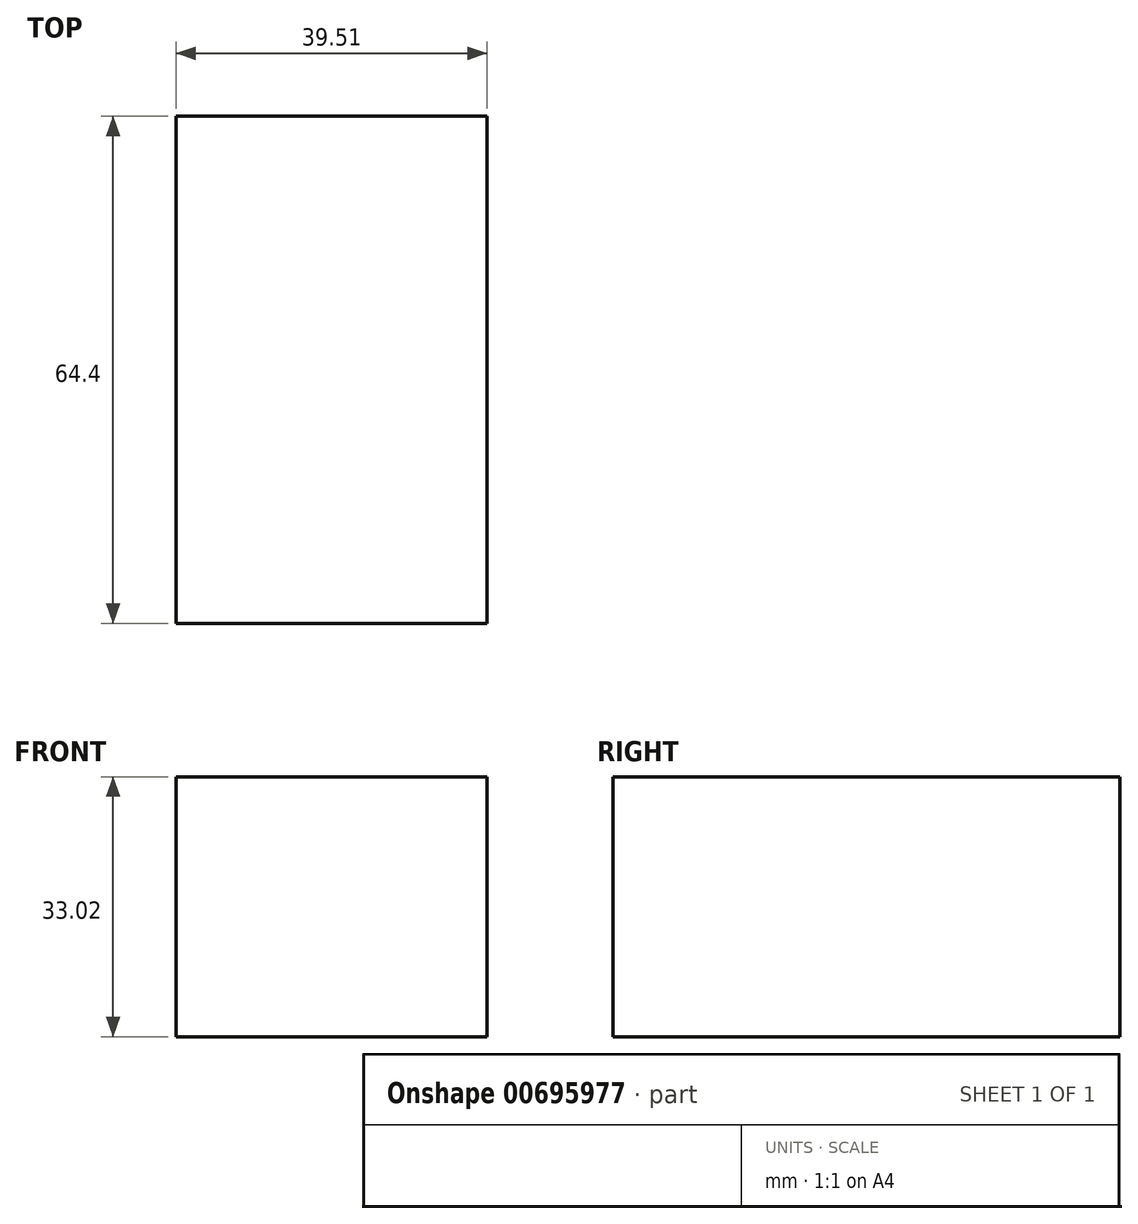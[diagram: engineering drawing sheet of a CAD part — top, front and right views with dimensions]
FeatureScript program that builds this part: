
annotation { "Feature Type Name" : "Feature", "Feature Type Description" : "" }
export const myFeature = defineFeature(function(context is Context, id is Id, definition is map)
    precondition{}
    {
        {
            var Q0;
            Q0=qCreatedBy(makeId("Top.planeOp"),FACE);
            var sketch = newSketch(context, id + "F0", { "sketchPlane" : qUnion([Q0])});
            skLineSegment(sketch, "E0.bottom", {"start": v(-58.37, 42.08) * mm, "end": v(-18.86, 42.08) * mm});
            skLineSegment(sketch, "E0.top", {"start": v(-58.37, -22.32) * mm, "end": v(-18.86, -22.32) * mm});
            skLineSegment(sketch, "E0.left", {"start": v(-58.37, 42.08) * mm, "end": v(-58.37, -22.32) * mm});
            skLineSegment(sketch, "E0.right", {"start": v(-18.86, 42.08) * mm, "end": v(-18.86, -22.32) * mm});
            skSolve(sketch);
        }
        {
            var Q0;
            Q0=makeQuery(id+"F0.imprint","IMPRINT",FACE,{"disambiguationData":[TD([[makeQuery(id+"F0.imprint","IMPRINT",EDGE,{"derivedFrom":sQuery(id+"F0.wireOp",EDGE,"E0.bottom")}),-1.0]])]});
            extrude(context, id + "F1", {"entities" : qUnion([Q0]), "depth" : 33.02 * mm, "offsetDistance" : 25.4 * mm});
        }
    });
